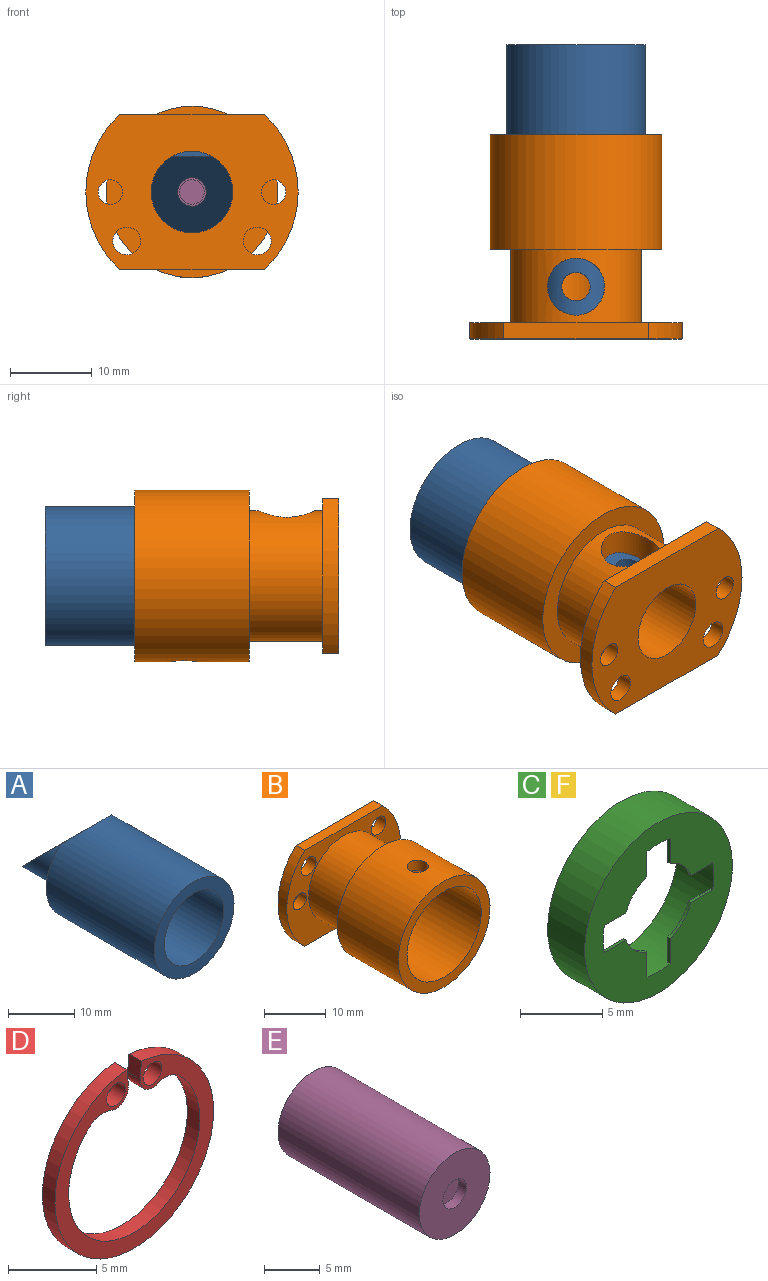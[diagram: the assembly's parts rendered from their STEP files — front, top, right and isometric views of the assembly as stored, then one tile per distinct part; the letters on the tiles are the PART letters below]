
ASSEMBLY  parts=6 mates=12
PART A: 11 faces, bbox 17x34x17 mm
  f0: cylinder r=8.5mm len=23mm, axis (0,1,0), area 1213.8mm2, adj f3,f4,f9
  f1: cylinder r=1.75mm len=8.6mm, axis (0,1,0), area 82.3mm2, adj f6,f7,f8
  f2: cylinder r=5mm len=11mm, axis (0,1,0), area 195.6mm2, adj f3,f7,f8,f10
  f3: plane 17x15.1mm, normal (0,1,0), area 134.5mm2, adj f0,f2,f9
  f4: plane 17x17mm, normal (0,-1,0), area 100.3mm2, adj f0,f5
  f5: cylinder r=6.35mm len=21mm, axis (0,-1,0), area 837.9mm2, adj f4,f6
  f6: plane 12.7x12.7mm, normal (0,-1,0), area 117.1mm2, adj f1,f5
  f7: cylinder r=1.75mm len=4.68mm, axis (0,0,1), area 39.3mm2, adj f1,f2,f8
  f8: plane 10x9.4mm, normal (0,0.71,0.71), area 94.7mm2, adj f1,f2,f7,f10
  f9: plane 10.71x1.9mm, normal (0,0.71,0.71), area 19.7mm2, adj f0,f3
  f10: plane 4.75x0.6mm, normal (0,1,0), area 1.9mm2, adj f2,f8
PART B: 19 faces, bbox 26x25x21 mm
  f0: cylinder r=10.5mm len=21mm, axis (0,-1,0), area 914.5mm2, adj f8,f16,f18
  f1: cylinder r=8.5mm len=17mm, axis (0,-1,0), area 631.8mm2, adj f8,f17,f18
  f2: cylinder r=5mm len=13mm, axis (0,-1,0), area 367mm2, adj f4,f9,f17
  f3: cylinder r=8mm len=16mm, axis (0,-1,0), area 412.9mm2, adj f5,f9,f16
  f4: plane 26x19mm, normal (0,1,0), area 334.7mm2, adj f2,f6,f7,f10,f11,f12,f13,f14
  f5: plane 26x19mm, normal (0,-1,0), area 212.2mm2, adj f3,f6,f7,f10,f11,f12,f13,f14
  f6: cylinder r=13mm len=19mm, axis (0,1,0), area 42.6mm2, adj f4,f5,f14,f15
  f7: cylinder r=13mm len=19mm, axis (0,1,0), area 42.6mm2, adj f4,f5,f14,f15
  f8: plane 21x21mm, normal (0,-1,0), area 119.4mm2, adj f0,f1
  f9: cylinder r=3.5mm len=7mm, axis (0,0,1), area 72.3mm2, adj f2,f3
  f10: cylinder r=1.5mm len=3mm, axis (0,-1,0), area 18.8mm2, adj f4,f5
  f11: cylinder r=1.7mm len=3.4mm, axis (0,-1,0), area 21.4mm2, adj f4,f5
  f12: cylinder r=1.7mm len=3.4mm, axis (0,-1,0), area 21.4mm2, adj f4,f5
  f13: cylinder r=1.5mm len=3mm, axis (0,-1,0), area 18.8mm2, adj f4,f5
  f14: plane 17.75x2mm, normal (0,0,-1), area 35.5mm2, adj f4,f5,f6,f7
  f15: plane 17.75x2mm, normal (0,0,1), area 35.5mm2, adj f4,f5,f6,f7
  f16: plane 21x21mm, normal (0,1,0), area 145.3mm2, adj f0,f3
  f17: plane 17x17mm, normal (0,-1,0), area 148.4mm2, adj f1,f2
  f18: cylinder r=1.7mm len=3.4mm, axis (0,0,-1), area 21.5mm2, adj f0,f1
PART C: 20 faces, bbox 12.7x3.2x12.7 mm
  f0: cylinder r=4.77mm len=9.53mm, axis (0,1,0), area 90.8mm2, adj f2,f3,f4,f5,f7,f8,f10,f11
  f1: cylinder r=6.35mm len=12.7mm, axis (0,1,0), area 126.9mm2, adj f2,f3
  f2: plane 12.7x12.7mm, normal (0,-1,0), area 84.4mm2, adj f0,f1,f4,f5,f6,f8,f9,f10
  f3: plane 12.7x12.7mm, normal (0,1,0), area 55.3mm2, adj f0,f1
  f4: plane 1.86x0.2mm, normal (1,0,0), area 0.4mm2, adj f0,f2,f6,f7
  f5: plane 1.86x0.2mm, normal (0,0,-1), area 0.4mm2, adj f0,f2,f6,f7
  f6: cylinder r=2.97mm len=1.8mm, axis (0,-1,0), area 0.5mm2, adj f2,f4,f5,f7
  f7: plane 3.66x3.66mm, normal (0,1,0), area 7.3mm2, adj f0,f4,f5,f6
  f8: plane 1.86x0.2mm, normal (-1,0,0), area 0.4mm2, adj f0,f2,f9,f11
  f9: cylinder r=2.97mm len=1.8mm, axis (0,-1,0), area 0.5mm2, adj f2,f8,f10,f11
  f10: plane 1.86x0.2mm, normal (0,0,-1), area 0.4mm2, adj f0,f2,f9,f11
  f11: plane 3.66x3.66mm, normal (0,1,0), area 7.3mm2, adj f0,f8,f9,f10
  f12: plane 1.86x0.2mm, normal (0,0,1), area 0.4mm2, adj f0,f2,f13,f15
  f13: cylinder r=2.97mm len=1.8mm, axis (0,-1,0), area 0.5mm2, adj f2,f12,f14,f15
  f14: plane 1.86x0.2mm, normal (-1,0,0), area 0.4mm2, adj f0,f2,f13,f15
  f15: plane 3.66x3.66mm, normal (0,1,0), area 7.3mm2, adj f0,f12,f13,f14
  f16: plane 1.86x0.2mm, normal (1,0,0), area 0.4mm2, adj f0,f2,f17,f19
  f17: cylinder r=2.97mm len=1.8mm, axis (0,-1,0), area 0.5mm2, adj f2,f16,f18,f19
  f18: plane 1.86x0.2mm, normal (0,0,1), area 0.4mm2, adj f0,f2,f17,f19
  f19: plane 3.66x3.66mm, normal (0,1,0), area 7.3mm2, adj f0,f16,f17,f18
PART D: 12 faces, bbox 12.7x1x12.7 mm
  f0: plane 1.19x1mm, normal (1,0,0.09), area 1.2mm2, adj f1,f8,f10,f11
  f1: cylinder r=6.35mm len=12.7mm, axis (0,1,0), area 38.7mm2, adj f0,f2,f10,f11
  f2: plane 1.19x1mm, normal (-1,0,0.09), area 1.2mm2, adj f1,f3,f10,f11
  f3: cylinder r=1mm len=1.4mm, axis (0,1,0), area 2.1mm2, adj f2,f4,f10,f11
  f4: cylinder r=1.61mm len=1.75mm, axis (0,1,0), area 1.9mm2, adj f3,f5,f10,f11
  f5: cylinder r=5.25mm len=10.5mm, axis (0,1,0), area 25mm2, adj f4,f6,f10,f11
  f6: cylinder r=1.61mm len=1.75mm, axis (0,1,0), area 1.9mm2, adj f5,f8,f10,f11
  f7: cylinder r=0.75mm len=1.5mm, axis (0,1,0), area 4.7mm2, adj f10,f11
  f8: cylinder r=1mm len=1.4mm, axis (0,1,0), area 2.1mm2, adj f0,f6,f10,f11
  f9: cylinder r=0.75mm len=1.5mm, axis (0,1,0), area 4.7mm2, adj f10,f11
  f10: plane 12.7x12.67mm, normal (0,-1,0), area 38.9mm2, adj f0,f1,f2,f3,f4,f5,f6,f7
  f11: plane 12.7x12.67mm, normal (0,1,0), area 38.9mm2, adj f0,f1,f2,f3,f4,f5,f6,f7
PART E: 5 faces, bbox 9x18x9 mm
  f0: cylinder r=4.5mm len=18mm, axis (0,-1,0), area 508.9mm2, adj f1,f2
  f1: plane 9x9mm, normal (0,1,0), area 63.6mm2, adj f0
  f2: plane 9x9mm, normal (0,-1,0), area 56.5mm2, adj f0,f3
  f3: cylinder r=1.5mm len=3mm, axis (0,-1,0), area 9.4mm2, adj f2,f4
  f4: plane 3x3mm, normal (0,-1,0), area 7.1mm2, adj f3
PART F: same geometry as C
PLACE A rot(axis=(1,0,0),180deg) t=(9.02,-21.33,9.35)mm
PLACE B rot(axis=(1,0,0),180deg) t=(9.02,-21.33,9.35)mm
PLACE C rot(axis=(0,-1,0),180deg) t=(9.02,-3.15,9.35)mm
PLACE D rot(axis=(-0.7,0.1,0.7),0deg) t=(9.02,13.67,9.35)mm
PLACE E rot(axis=(0,-1,0),146.8deg) t=(9.02,-6.13,9.35)mm
PLACE F rot(axis=(0,0,-1),180deg) t=(9.02,8.89,9.35)mm
MATE cylindrical A.f0 <-> B.f1  axis (0,-1,0) through (9.02,3.17,9.35)mm
MATE cylindrical A.f5 <-> D.f1  axis (0,1,0) through (9.02,4.17,9.35)mm
MATE planar C.f9 <-> E.f0  axis (0,-1,0) through (9.02,-6.33,9.35)mm
MATE cylindrical B.f9 <-> A.f7  axis (0,0,-1) through (9.02,-14.93,17.39)mm
MATE cylindrical A.f5 <-> F.f1  axis (0,1,0) through (9.02,14.67,9.35)mm
MATE planar A.f0 <-> C.f9  axis (0,1,0) through (9.02,-6.33,9.35)mm
MATE cylindrical E.f0 <-> F.f0  axis (0,-1,0) through (9.02,2.87,9.35)mm
MATE planar B.f1 <-> A.f3  axis (0,1,0) through (9.02,-8.33,9.35)mm
MATE pin_slot D.f1 <-> A.f5  axis (0,1,0) through (9.02,13.17,9.35)mm
MATE planar F.f15 <-> E.f0  axis (0,-1,0) through (6.34,11.87,6.68)mm
MATE parallel B.f15 <-> C.f12  axis (0,0,-1) through (9.02,-20.33,-0.15)mm
MATE cylindrical E.f0 <-> C.f0  axis (0,-1,0) through (9.02,2.87,9.35)mm
